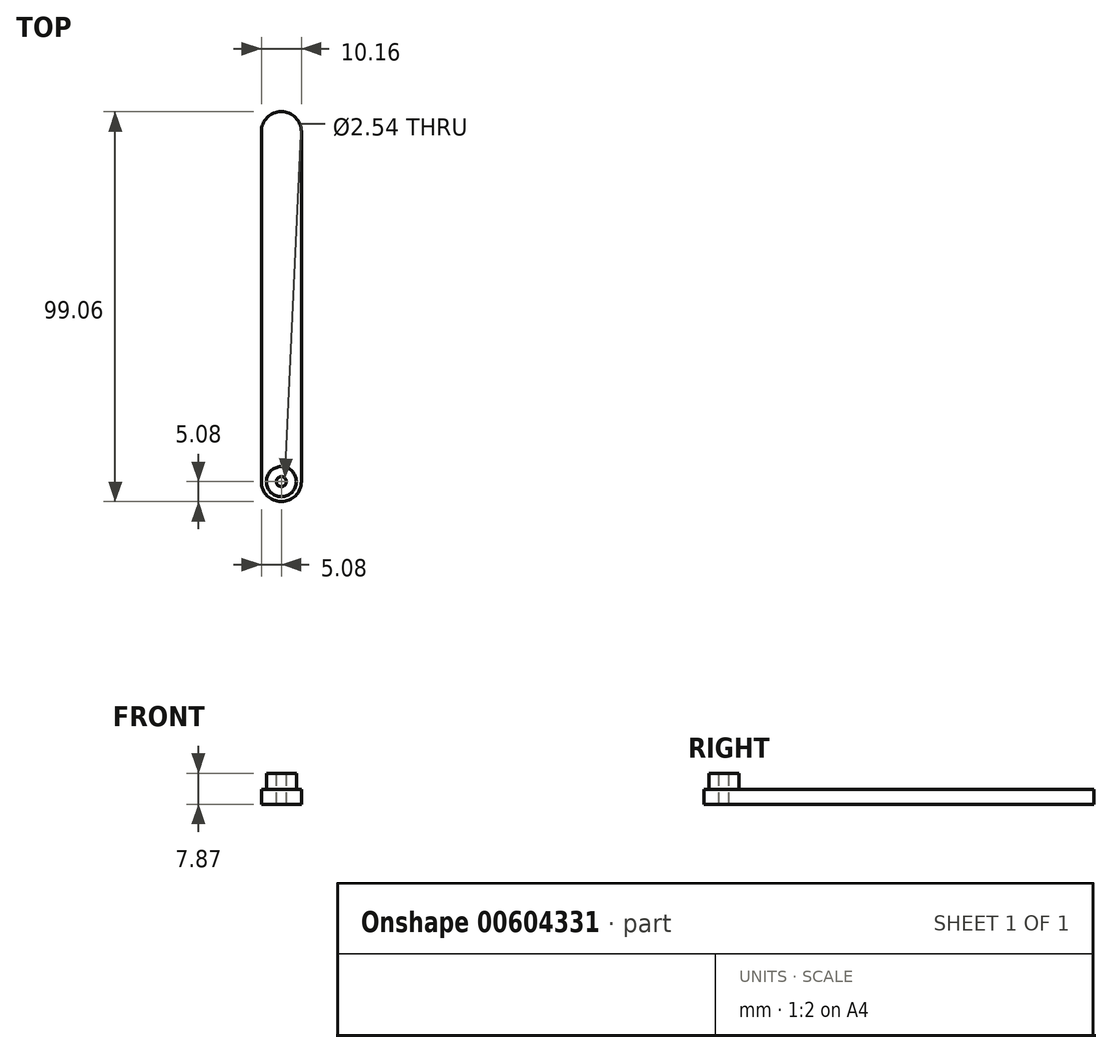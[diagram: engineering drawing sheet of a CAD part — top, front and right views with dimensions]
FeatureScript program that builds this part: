
annotation { "Feature Type Name" : "Feature", "Feature Type Description" : "" }
export const myFeature = defineFeature(function(context is Context, id is Id, definition is map)
    precondition{}
    {
        {
            var Q0;
            Q0=qCreatedBy(makeId("Top.planeOp"),FACE);
            var sketch = newSketch(context, id + "F0", { "sketchPlane" : qUnion([Q0])});
            skArc(sketch, "E0", {"start": v(0, 5.08) * mm, "mid": v(5.08, 0) * mm, "end": v(10.16, 5.08) * mm});
            skArc(sketch, "E1", {"start": v(10.16, 93.98) * mm, "mid": v(5.08, 99.06) * mm, "end": v(0, 93.98) * mm});
            skLineSegment(sketch, "E2", {"start": v(0, 93.98) * mm, "end": v(0, 5.08) * mm});
            skLineSegment(sketch, "E3", {"start": v(10.16, 93.98) * mm, "end": v(10.16, 5.08) * mm});
            skSolve(sketch);
        }
        {
            var Q0;
            Q0=qSketchRegion(id+"F0",true);
            extrude(context, id + "F1", {"entities" : qUnion([Q0]), "depth" : 3.8 * mm, "offsetDistance" : 25.4 * mm});
        }
        {
            var Q0;
            Q0=makeQuery(id+"F1.opExtrude","CAP_FACE",FACE,{"disambiguationData":[OSD([sQuery(id+"F0.wireOp",EDGE,"E0"),sQuery(id+"F0.wireOp",EDGE,"E1"),sQuery(id+"F0.wireOp",EDGE,"E2"),sQuery(id+"F0.wireOp",EDGE,"E3")])],"isStart":false});
            var sketch = newSketch(context, id + "F2", { "sketchPlane" : qUnion([Q0])});
            skCircle(sketch, "E4", {"center": v(5.08, 5.08) * mm, "radius": 3.8 * mm});
            skSolve(sketch);
        }
        {
            var Q0;
            Q0=qSketchRegion(id+"F2",true);
            extrude(context, id + "F3", {"entities" : qUnion([Q0]), "operationType" : NewBodyOperationType.ADD, "depth" : 4.06 * mm, "offsetDistance" : 25.4 * mm});
        }
        {
            var Q0;
            Q0=makeQuery(id+"F3.opExtrude","CAP_FACE",FACE,{"disambiguationData":[OSD([sQuery(id+"F2.wireOp",EDGE,"E4")])],"isStart":false});
            var sketch = newSketch(context, id + "F4", { "sketchPlane" : qUnion([Q0])});
            skPoint(sketch, "E5", {"position": v(5.08, 5.08) * mm});
            skSolve(sketch);
        }
        {
            var Q0;
            Q0=sQuery(id+"F4.wireOp",VERTEX,"E5");
            var Q1;
            Q1=makeQuery(id+"F1.opExtrude","SWEPT_BODY",BODY,{"disambiguationData":[OSD([sQuery(id+"F0.wireOp",EDGE,"E0"),sQuery(id+"F0.wireOp",EDGE,"E1"),sQuery(id+"F0.wireOp",EDGE,"E2"),sQuery(id+"F0.wireOp",EDGE,"E3")])]});
            hole(context, id + "F5", {"style" : HoleStyle.SIMPLE, "endStyle" : HoleEndStyle.BLIND, "holeDiameter" : 2.54 * mm, "majorDiameter" : 6.35 * mm, "holeDepth" : 12.7 * mm, "isTappedThrough" : true, "tappedDepth" : 12.7 * mm, "tapClearance" : 3, "startFromSketch" : true, "locations" : qUnion([Q0]), "scope" : qUnion([Q1])});
        }
    });
